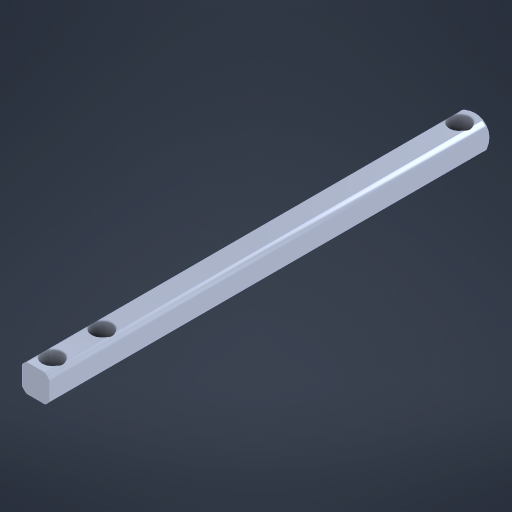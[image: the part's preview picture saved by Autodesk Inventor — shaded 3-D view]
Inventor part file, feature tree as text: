
AUTODESK INVENTOR PART (.ipt)
format: ipt  version: 2024 (Build 280153000, 153)  size: 331,264 bytes
history: native  units: in
note: dims shown in document units (in); Inventor stores cm internally (conversion verified against a paired STEP export)
features: other x50, sketch x4, extrude x2, hole x2, thicken_offset x1
ambient origin geometry x8: Origin, YZ Plane, XZ Plane, XY Plane, X Axis, Y Axis, Z Axis, Center Point
bodies: Solid1 (feature_tree)
feature tree (59):
  other  "Table"
  other  "Shaft HS 0.5 in"
  other  "Shaft HS 1.0 in"
  other  "Shaft HS 1.5 in"
  other  "Shaft HS 2.0 in"
  other  "Shaft HS 2.5 in"
  other  "Shaft HS 3.0 in"
  other  "Shaft HS 3.5 in"
  other  "Shaft HS 4.0 in"
  other  "Shaft HS 4.5 in"
  other  "Shaft HS 5.0 in"
  other  "Shaft HS 5.5 in"
  other  "Shaft HS 6.0 in"
  other  "Shaft HS 6.5 in"
  other  "Shaft HS 7.0 in"
  other  "Shaft HS 7.5 in"
  other  "Shaft HS 8.0 in"
  other  "Shaft HS 8.5 in"
  other  "Shaft HS 9.0 in"
  other  "Shaft HS 9.5 in"
  other  "Shaft HS 10.0 in"
  other  "Shaft HS 10.5 in"
  other  "Shaft HS 11.0 in"
  other  "Shaft HS 11.5 in"
  other  "Shaft HS 12.0 in"
  other  "Shaft HS 12.5 in"
  other  "Shaft HS 13.0 in"
  other  "Shaft HS 13.5 in"
  other  "Shaft HS 14.0 in"
  other  "Shaft HS 14.5 in"
  other  "Shaft HS 15.0 in"
  other  "Shaft HS 15.5 in"
  other  "Shaft HS 16.0 in"
  other  "Shaft HS 16.5 in"
  other  "Shaft HS 17.0 in"
  other  "Shaft HS 17.5 in"
  other  "Shaft HS 18.0 in"
  other  "Shaft HS 18.5 in"
  other  "Shaft HS 19.0 in"
  other  "Shaft HS 19.5 in"
  other  "Shaft HS 20.0 in"
  other  "Shaft HS 20.5 in"
  other  "Shaft HS 21.0 in"
  other  "Shaft HS 21.5 in"
  other  "Shaft HS 22.0 in"
  other  "Shaft HS 22.5 in"
  other  "Shaft HS 23.0 in"
  other  "Shaft HS 23.5 in"
  other  "Shaft HS 24.0 in"
  extrude  "Extrusion1"  Depth=12.1875in
  thicken_offset  "Thicken1"
  extrude  "Extrusion2"  Depth=20.125in
  hole  "Hole1"  [1 undecoded]
  hole  "Hole2"  [1 undecoded]
  sketch  "Sketch2"  dims[d0=0.0625in d1=0.0in d2=12.1875in]
  sketch  "Sketch3"  dims[d3=12.125in d4=20.125in]
  sketch  "Sketch6"  dims[d5=0.0in d9=0.15in]
  sketch  "Sketch7"  dims[d11=0.1875in d12=0.75in d13=0.375in d14=0.25in d15=0.5635in d16=1.0in d17=0.8108in d18=3.7in d19=3.25in d20=0.1875in d21=0.75in d22=0.375in d23=0.25in d24=0.5635in d25=1.0in d26=0.8108in]
  other  "Cut-Revolve3"
note: 2 required parameter values undecoded (feature->parameter linkage not recoverable at this tier; creation-order binding heuristic only, values carry confidence <= 0.55)
